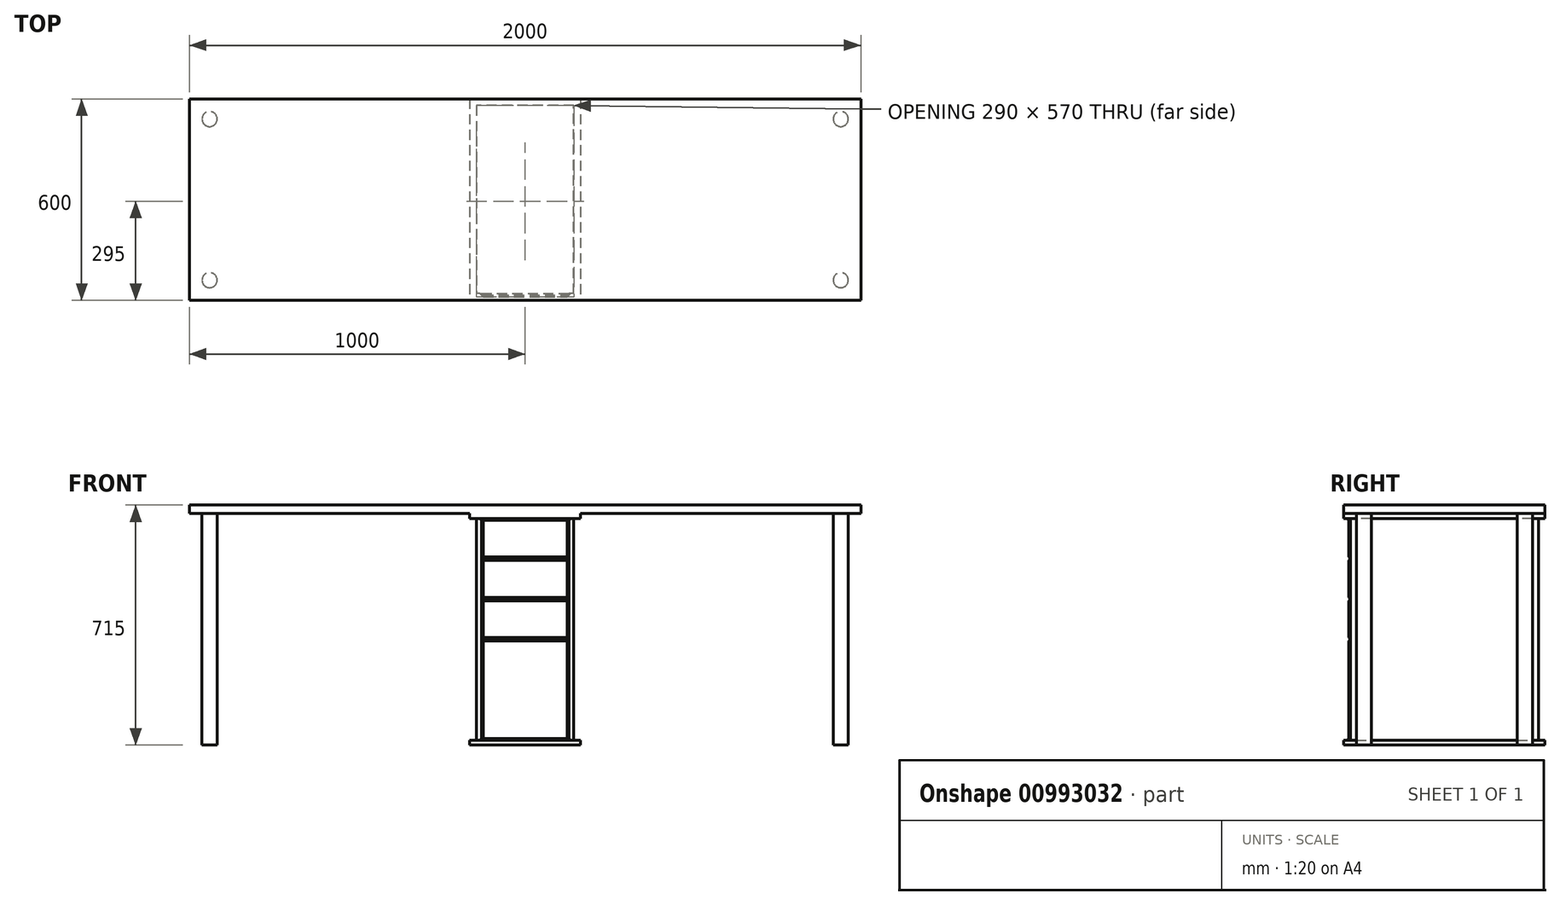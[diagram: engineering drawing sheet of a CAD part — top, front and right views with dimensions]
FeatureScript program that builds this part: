
annotation { "Feature Type Name" : "Feature", "Feature Type Description" : "" }
export const myFeature = defineFeature(function(context is Context, id is Id, definition is map)
    precondition{}
    {
        {
            var Q0;
            Q0=qCreatedBy(makeId("Top.planeOp"),FACE);
            var sketch = newSketch(context, id + "F0", { "sketchPlane" : qUnion([Q0])});
            skLineSegment(sketch, "E0.bottom", {"start": v(165, -300) * mm, "end": v(-165, -300) * mm});
            skLineSegment(sketch, "E0.top", {"start": v(165, 300) * mm, "end": v(-165, 300) * mm});
            skLineSegment(sketch, "E0.left", {"start": v(165, -300) * mm, "end": v(165, 300) * mm});
            skLineSegment(sketch, "E0.right", {"start": v(-165, -300) * mm, "end": v(-165, 300) * mm});
            skPoint(sketch, "E0.middle", {"position": v(0, 0) * mm});
            skSolve(sketch);
        }
        {
            var Q0;
            Q0 = qSketchRegion(id + "F0", true);
            extrude(context, id + "F1", {"entities" : qUnion([Q0]), "depth" : 15 * mm, "offsetDistance" : 25 * mm});
        }
        {
            var Q0;
            Q0=makeQuery(id+"F1.opExtrude","CAP_FACE",FACE,{"disambiguationData":[OSD([sQuery(id+"F0.wireOp",EDGE,"E0.bottom"),sQuery(id+"F0.wireOp",EDGE,"E0.top"),sQuery(id+"F0.wireOp",EDGE,"E0.left"),sQuery(id+"F0.wireOp",EDGE,"E0.right")])],"isStart":false});
            var sketch = newSketch(context, id + "F2", { "sketchPlane" : qUnion([Q0])});
            skLineSegment(sketch, "E1.0", {"start": v(145, -280) * mm, "end": v(145, 280) * mm});
            skLineSegment(sketch, "E1.2", {"start": v(-145, 280) * mm, "end": v(-145, -280) * mm});
            skLineSegment(sketch, "E1.3", {"start": v(145, 280) * mm, "end": v(-145, 280) * mm});
            skLineSegment(sketch, "E2.0", {"start": v(130, -265) * mm, "end": v(130, 265) * mm});
            skLineSegment(sketch, "E2.2", {"start": v(-130, 265) * mm, "end": v(-130, -265) * mm});
            skLineSegment(sketch, "E2.3", {"start": v(130, 265) * mm, "end": v(-130, 265) * mm});
            skLineSegment(sketch, "E3", {"start": v(130, -265) * mm, "end": v(130, -280) * mm});
            skLineSegment(sketch, "E4", {"start": v(-130, -265) * mm, "end": v(-130, -280) * mm});
            skLineSegment(sketch, "E5", {"start": v(145, -280) * mm, "end": v(130, -280) * mm});
            skLineSegment(sketch, "E6", {"start": v(-130, -280) * mm, "end": v(-145, -280) * mm});
            skSolve(sketch);
        }
        {
            var Q0;
            Q0 = qSketchRegion(id + "F2", true);
            extrude(context, id + "F3", {"entities" : qUnion([Q0]), "operationType" : NewBodyOperationType.ADD, "depth" : 660 * mm, "offsetDistance" : 25 * mm});
        }
        {
            var Q0;
            Q0=makeQuery(id+"F3.opExtrude","CAP_FACE",FACE,{"disambiguationData":[OSD([sQuery(id+"F2.wireOp",EDGE,"E1.0"),sQuery(id+"F2.wireOp",EDGE,"E1.2"),sQuery(id+"F2.wireOp",EDGE,"E1.3"),sQuery(id+"F2.wireOp",EDGE,"E2.0"),sQuery(id+"F2.wireOp",EDGE,"E2.2"),sQuery(id+"F2.wireOp",EDGE,"E2.3"),sQuery(id+"F2.wireOp",EDGE,"E3"),sQuery(id+"F2.wireOp",EDGE,"E4"),sQuery(id+"F2.wireOp",EDGE,"E5"),sQuery(id+"F2.wireOp",EDGE,"E6")])],"isStart":false});
            var sketch = newSketch(context, id + "F4", { "sketchPlane" : qUnion([Q0])});
            skLineSegment(sketch, "E7.0", {"start": v(-165, -300) * mm, "end": v(165, -300) * mm});
            skLineSegment(sketch, "E7.1", {"start": v(-165, 300) * mm, "end": v(-165, -300) * mm});
            skLineSegment(sketch, "E7.2", {"start": v(-165, 300) * mm, "end": v(165, 300) * mm});
            skLineSegment(sketch, "E7.3", {"start": v(165, 300) * mm, "end": v(165, -300) * mm});
            skSolve(sketch);
        }
        {
            var Q0;
            Q0 = qSketchRegion(id + "F4", true);
            extrude(context, id + "F5", {"entities" : qUnion([Q0]), "operationType" : NewBodyOperationType.ADD, "depth" : 15 * mm, "offsetDistance" : 25 * mm});
        }
        {
            var Q0;
            Q0=makeQuery(id+"F3.opExtrude","SWEPT_FACE",FACE,{"disambiguationData":[OSD([sQuery(id+"F2.wireOp",EDGE,"E2.3")])]});
            var sketch = newSketch(context, id + "F6", { "sketchPlane" : qUnion([Q0])});
            skLineSegment(sketch, "E8.bottom", {"start": v(-130, 675) * mm, "end": v(130, 675) * mm});
            skLineSegment(sketch, "E8.top", {"start": v(-130, 555) * mm, "end": v(130, 555) * mm});
            skLineSegment(sketch, "E8.left", {"start": v(-130, 675) * mm, "end": v(-130, 555) * mm});
            skLineSegment(sketch, "E8.right", {"start": v(130, 675) * mm, "end": v(130, 555) * mm});
            skLineSegment(sketch, "E9.top", {"start": v(-130, 435) * mm, "end": v(130, 435) * mm});
            skLineSegment(sketch, "E9.left", {"start": v(-130, 555) * mm, "end": v(-130, 435) * mm});
            skLineSegment(sketch, "E9.right", {"start": v(130, 555) * mm, "end": v(130, 435) * mm});
            skLineSegment(sketch, "E10.top", {"start": v(-130, 315) * mm, "end": v(130, 315) * mm});
            skLineSegment(sketch, "E10.left", {"start": v(-130, 435) * mm, "end": v(-130, 315) * mm});
            skLineSegment(sketch, "E10.right", {"start": v(130, 435) * mm, "end": v(130, 315) * mm});
            skLineSegment(sketch, "E11.bottom", {"start": v(-130, 315) * mm, "end": v(118.2, 315) * mm});
            skLineSegment(sketch, "E11.top", {"start": v(-130, 15) * mm, "end": v(118.2, 15) * mm});
            skLineSegment(sketch, "E11.left", {"start": v(-130, 315) * mm, "end": v(-130, 15) * mm});
            skSolve(sketch);
        }
        {
            var Q0;
            {var subQ1=sQuery(id+"F6.wireOp",EDGE,"E10.top");Q0=makeQuery(id+"F6.imprint","IMPRINT",FACE,{"disambiguationData":[TD([[makeQuery(id+"F6.imprint","IMPRINT",EDGE,{"derivedFrom":subQ1}),-1.0]])]});}
            extrude(context, id + "F7", {"entities" : qUnion([Q0]), "operationType" : NewBodyOperationType.ADD, "depth" : 550 * mm, "offsetDistance" : 25 * mm});
        }
        {
            var Q0;
            Q0=makeQuery(id+"F7.opExtrude","CAP_FACE",FACE,{"disambiguationData":[OSD([sQuery(id+"F2.wireOp",EDGE,"E2.0"),sQuery(id+"F2.wireOp",EDGE,"E2.3"),sQuery(id+"F6.wireOp",EDGE,"E10.top"),sQuery(id+"F6.wireOp",EDGE,"E11.bottom"),sQuery(id+"F6.wireOp",EDGE,"E11.top"),sQuery(id+"F6.wireOp",EDGE,"E11.left")])],"isStart":false});
            chamfer(context, id + "F8", {"entities" : qUnion([Q0]), "width" : 5 * mm, "tangentPropagation" : true});
        }
        {
            var Q0;
            Q0=makeQuery(id+"F6.imprint","IMPRINT",FACE,{"disambiguationData":[TD([[makeQuery(id+"F6.imprint","IMPRINT",EDGE,{"derivedFrom":sQuery(id+"F6.wireOp",EDGE,"E9.top")}),-1.0]])]});
            extrude(context, id + "F9", {"entities" : qUnion([Q0]), "operationType" : NewBodyOperationType.ADD, "depth" : 550 * mm, "offsetDistance" : 25 * mm});
        }
        {
            var Q0;
            Q0=makeQuery(id+"F9.opExtrude","CAP_FACE",FACE,{"disambiguationData":[OSD([sQuery(id+"F6.wireOp",EDGE,"E9.top"),sQuery(id+"F6.wireOp",EDGE,"E10.top"),sQuery(id+"F6.wireOp",EDGE,"E10.left"),sQuery(id+"F6.wireOp",EDGE,"E10.right"),sQuery(id+"F6.wireOp",EDGE,"E11.bottom")])],"isStart":false});
            chamfer(context, id + "F10", {"entities" : qUnion([Q0]), "width" : 5 * mm, "tangentPropagation" : true});
        }
        {
            var Q0;
            Q0=makeQuery(id+"F6.imprint","IMPRINT",FACE,{"disambiguationData":[TD([[makeQuery(id+"F6.imprint","IMPRINT",EDGE,{"derivedFrom":sQuery(id+"F6.wireOp",EDGE,"E8.top")}),-1.0]])]});
            extrude(context, id + "F11", {"entities" : qUnion([Q0]), "operationType" : NewBodyOperationType.ADD, "depth" : 550 * mm, "offsetDistance" : 25 * mm});
        }
        {
            var Q0;
            Q0=makeQuery(id+"F11.opExtrude","CAP_FACE",FACE,{"disambiguationData":[OSD([sQuery(id+"F6.wireOp",EDGE,"E8.top"),sQuery(id+"F6.wireOp",EDGE,"E9.left"),sQuery(id+"F6.wireOp",EDGE,"E9.right"),sQuery(id+"F6.wireOp",EDGE,"E9.top")])],"isStart":false});
            chamfer(context, id + "F12", {"entities" : qUnion([Q0]), "width" : 5 * mm, "tangentPropagation" : true});
        }
        {
            var Q0;
            Q0=makeQuery(id+"F6.imprint","IMPRINT",FACE,{"disambiguationData":[TD([[makeQuery(id+"F6.imprint","IMPRINT",EDGE,{"derivedFrom":sQuery(id+"F6.wireOp",EDGE,"E8.bottom")}),1.0]])]});
            extrude(context, id + "F13", {"entities" : qUnion([Q0]), "operationType" : NewBodyOperationType.ADD, "depth" : 550 * mm, "offsetDistance" : 25 * mm});
        }
        {
            var Q0;
            Q0=makeQuery(id+"F13.opExtrude","CAP_FACE",FACE,{"disambiguationData":[OSD([sQuery(id+"F6.wireOp",EDGE,"E8.bottom"),sQuery(id+"F6.wireOp",EDGE,"E8.left"),sQuery(id+"F6.wireOp",EDGE,"E8.right"),sQuery(id+"F6.wireOp",EDGE,"E8.top")])],"isStart":false});
            chamfer(context, id + "F14", {"entities" : qUnion([Q0]), "width" : 5 * mm, "tangentPropagation" : true});
        }
        {
            var Q0;
            Q0=makeQuery(id+"F5.opExtrude","CAP_FACE",FACE,{"disambiguationData":[OSD([sQuery(id+"F4.wireOp",EDGE,"E7.0"),sQuery(id+"F4.wireOp",EDGE,"E7.1"),sQuery(id+"F4.wireOp",EDGE,"E7.2"),sQuery(id+"F4.wireOp",EDGE,"E7.3")])],"isStart":false});
            var sketch = newSketch(context, id + "F15", { "sketchPlane" : qUnion([Q0])});
            skLineSegment(sketch, "E12.bottom", {"start": v(-1000, 300) * mm, "end": v(1000, 300) * mm});
            skLineSegment(sketch, "E12.top", {"start": v(-1000, -300) * mm, "end": v(1000, -300) * mm});
            skLineSegment(sketch, "E12.left", {"start": v(-1000, 300) * mm, "end": v(-1000, -300) * mm});
            skLineSegment(sketch, "E12.right", {"start": v(1000, 300) * mm, "end": v(1000, -300) * mm});
            skPoint(sketch, "E12.middle", {"position": v(0, 0) * mm});
            skSolve(sketch);
        }
        {
            var Q0;
            {var subQ2=sQuery(id+"F15.wireOp",EDGE,"E12.left");Q0=makeQuery(id+"F15.imprint","IMPRINT",FACE,{"disambiguationData":[TD([[makeQuery(id+"F15.imprint","IMPRINT",EDGE,{"derivedFrom":subQ2}),1.0]])]});}
            var Q1;
            {var subQ1=makeQuery(id+"F5.opExtrude","CAP_EDGE",EDGE,{"disambiguationData":[OSD([sQuery(id+"F4.wireOp",EDGE,"E7.1")])],"isStart":false});Q1=makeQuery(id+"F15.imprint","IMPRINT",FACE,{"disambiguationData":[TD([[makeQuery(id+"F15.imprint","IMPRINT",EDGE,{"derivedFrom":subQ1}),1.0]])]});}
            var Q2;
            {var subQ2=sQuery(id+"F15.wireOp",EDGE,"E12.right");Q2=makeQuery(id+"F15.imprint","IMPRINT",FACE,{"disambiguationData":[TD([[makeQuery(id+"F15.imprint","IMPRINT",EDGE,{"derivedFrom":subQ2}),-1.0]])]});}
            extrude(context, id + "F16", {"entities" : qUnion([Q0, Q1, Q2]), "operationType" : NewBodyOperationType.ADD, "depth" : 25 * mm, "offsetDistance" : 25 * mm});
        }
        {
            var Q0;
            {var subQ0=sQuery(id+"F15.wireOp",EDGE,"E12.bottom");var subQ1=sQuery(id+"F15.wireOp",EDGE,"E12.right");var subQ2=sQuery(id+"F15.wireOp",EDGE,"E12.top");Q0=makeQuery(id+"F16.boolean.opBoolean","SPLIT",FACE,{"disambiguationData":[TD([makeQuery(id+"F5.opExtrude","SWEPT_FACE",FACE,{"disambiguationData":[OSD([sQuery(id+"F4.wireOp",EDGE,"E7.3")])]})])],"derivedFrom":makeQuery(id+"F16.opExtrude","CAP_FACE",FACE,{"disambiguationData":[OSD([subQ0,subQ2,sQuery(id+"F15.wireOp",EDGE,"E12.left"),subQ1])],"isStart":true})});}
            var sketch = newSketch(context, id + "F17", { "sketchPlane" : qUnion([Q0])});
            skCircle(sketch, "E13", {"center": v(940, 240) * mm, "radius": 22.5 * mm});
            skCircle(sketch, "E14", {"center": v(940, -240) * mm, "radius": 22.5 * mm});
            skSolve(sketch);
        }
        {
            var Q0;
            Q0 = qSketchRegion(id + "F17", true);
            extrude(context, id + "F18", {"entities" : qUnion([Q0]), "operationType" : NewBodyOperationType.ADD, "depth" : 690 * mm, "offsetDistance" : 25 * mm});
        }
        {
            var Q0;
            {var subQ0=sQuery(id+"F15.wireOp",EDGE,"E12.bottom");var subQ1=sQuery(id+"F15.wireOp",EDGE,"E12.top");var subQ2=sQuery(id+"F15.wireOp",EDGE,"E12.left");Q0=makeQuery(id+"F16.boolean.opBoolean","SPLIT",FACE,{"disambiguationData":[TD([makeQuery(id+"F5.opExtrude","SWEPT_FACE",FACE,{"disambiguationData":[OSD([sQuery(id+"F4.wireOp",EDGE,"E7.1")])]})])],"derivedFrom":makeQuery(id+"F16.opExtrude","CAP_FACE",FACE,{"disambiguationData":[OSD([subQ0,subQ1,subQ2,sQuery(id+"F15.wireOp",EDGE,"E12.right")])],"isStart":true})});}
            var sketch = newSketch(context, id + "F19", { "sketchPlane" : qUnion([Q0])});
            skCircle(sketch, "E15", {"center": v(-940, -240) * mm, "radius": 22.5 * mm});
            skCircle(sketch, "E16", {"center": v(-940, 240) * mm, "radius": 22.5 * mm});
            skSolve(sketch);
        }
        {
            var Q0;
            Q0 = qSketchRegion(id + "F19", true);
            extrude(context, id + "F20", {"entities" : qUnion([Q0]), "operationType" : NewBodyOperationType.ADD, "depth" : 690 * mm, "offsetDistance" : 25 * mm});
        }
    });
